# Revit family: 3DM_Domekt-CF-700-V-E-R1
name_source: partatom
category: Mechanical Equipment
revit_build: Autodesk Revit 2016 (Build: 20151007_0715(x64)
units: mm (PartAtom-declared; Revit-internal decimal feet)

## family parameters
Always vertical = Yes
Cut with Voids When Loaded = No
OmniClass Number = 23.75.00.00
OmniClass Title = Climate Control (HVAC)
Part Type = Normal
Room Calculation Point = No
Round Connector Dimension = Use Diameter
Shared = No
Work Plane-Based = No

## types (1)
- DOMEKT CF 700 V_Right
    Currency = Euro
    Current = 12 A
    Data sheet = http://www.komfovent.com
    Electrical potential = 230 V
    Frequency = 50 Hz
    Functional diagram = http://www.komfovent.com
    Installation manual = http://www.komfovent.com
    Manufacturer = Komfovent
    Model = Domekt-CF-700-V-E-R1
    Power = 0 W
    Quantity Type = Number
    Type Image = <None>
    URL = www.komfovent.com
    Unit weight = 95.00 kg
    Wiring diagram = http://www.komfovent.com

## geometry (parser evidence)
native form markers: Blend x4, Sweep x3
no freeform markers — native parametric forms only
